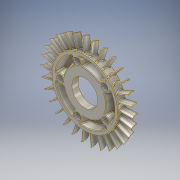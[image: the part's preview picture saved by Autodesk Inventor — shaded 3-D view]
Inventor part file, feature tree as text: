
AUTODESK INVENTOR PART (.ipt)
format: ipt  version: 2019 (Build 230136000, 136)  size: 2,415,104 bytes
history: native  units: mm
features: fillet x9, sketch x7, other x5, extrude x5, hole x3, pattern_circular x2, direct_edit x2, revolve x2, delete_face x1, plane x1, loft x1
ambient origin geometry x8: Origin, YZ Plane, XZ Plane, XY Plane, X Axis, Y Axis, Z Axis, Center Point
bodies: Solid1 (feature_tree)
feature tree (38):
  other  "Table"
  other  "Rear Compression Fan 01"
  other  "Rear Compression Fan 02"
  other  "Rear Compression Fan 03"
  extrude  "Extrusion1"  Depth=19.0mm
  extrude  "Extrusion2"  Depth=10.0mm
  fillet  "Fillet2"  Radius=44.0mm
  pattern_circular  "Circular Pattern2"  Count=5 Angle=360.0deg
  extrude  "Extrusion3"  Depth=300.0mm TaperAngle=0.0deg
  fillet  "Fillet1"  Radius=165.0mm
  hole  "Hole1"  [1 undecoded]
  hole  "Hole2"  [1 undecoded]
  hole  "Hole3"  [1 undecoded]
  pattern_circular  "Circular Pattern1"  [2 undecoded]
  direct_edit  "Direct Edit1"
  extrude  "Extrusion4"  Depth=1.5mm
  fillet  "Fillet3"  Radius=1.5mm
  fillet  "Fillet4"  Radius=1.5mm
  fillet  "Fillet5"  Radius=52.5mm
  fillet  "Fillet6"  Radius=8.5mm
  delete_face  "Delete Face1"
  plane  "Work Plane2"
  loft  "Loft1"
  fillet  "Fillet7"  Radius=12.0mm
  extrude  "Extrusion5"  Depth=128.0mm
  fillet  "Fillet8"  [1 undecoded]
  fillet  "Fillet9"  [1 undecoded]
  direct_edit  "Direct Edit2"
  sketch  "Sketch1"  dims[d0=119.0mm d1=19.0mm d2=-2.617994mm]
  sketch  "Sketch2"  dims[d3=1.0mm]
  sketch  "Sketch3"  dims[d79=10.0mm d80=10.0mm d6=68.0mm d7=6.0mm d8=4.0mm d9=2.0mm d10=90.0deg d11=8.0mm d12=0.0mm d13=10.0mm d14=10.0mm]
  sketch  "Sketch4"  dims[d15=46.0mm d16=6.0mm d17=4.0mm d18=2.0mm d19=90.0deg d20=8.0mm d21=0.0mm d22=44.0mm]
  sketch  "Sketch5"  dims[d23=12.0mm d24=6.0mm d25=4.0mm d26=2.0mm d27=90.0deg d28=8.0mm d29=0.0mm d30=50.0mm d31=360.0deg]
  sketch  "Sketch6"  dims[d33=1.5mm d34=300.0mm d35=0.0mm d36=165.0mm]
  other  "Edges1"
  sketch  "Sketch7"  dims[d37=111.0mm d38=-2.617994mm d39=300.0mm d40=360.0deg d42=1.5mm d51=12.0mm d52=-2.617994mm d53=1.5mm d54=1.5mm d55=1.5mm d56=1.5mm d58=52.5mm d60=8.5mm d61=3.5mm d62=12.0mm d64=128.0mm d65=0.0mm d66=90.0deg d67=0.0mm d68=90.0deg d69=1.5mm d70=112.895mm d71=1.0mm d72=0.0mm d73=2.0mm d74=2.0mm d76=38.0mm d77=0.174533mm d78=-1.22173mm]
  revolve  "Rotate1"  [1 undecoded]
  revolve  "Rotate2"  [1 undecoded]
note: 9 required parameter values undecoded (feature->parameter linkage not recoverable at this tier; creation-order binding heuristic only, values carry confidence <= 0.55)